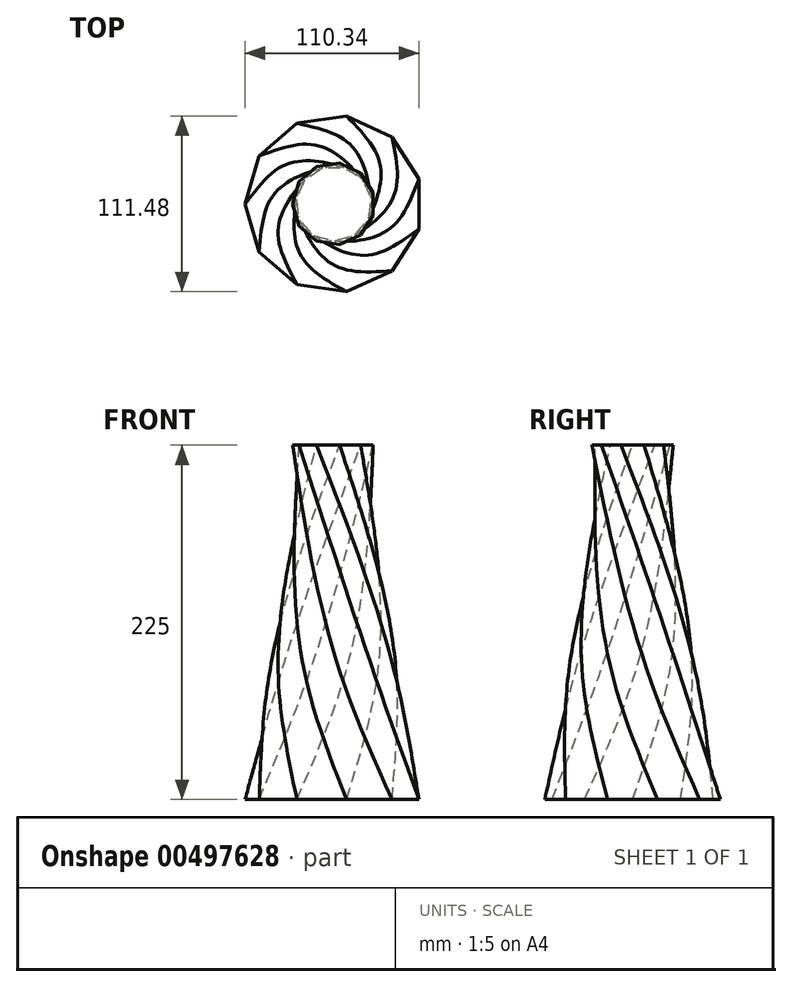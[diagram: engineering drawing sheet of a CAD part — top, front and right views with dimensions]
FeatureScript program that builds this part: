
annotation { "Feature Type Name" : "Feature", "Feature Type Description" : "" }
export const myFeature = defineFeature(function(context is Context, id is Id, definition is map)
    precondition{}
    {
        {
            var Q0;
            Q0=qCreatedBy(makeId("Top.planeOp"),FACE);
            var sketch = newSketch(context, id + "F0", { "sketchPlane" : qUnion([Q0])});
            skCircle(sketch, "E0.cCircle", {"center": v(0, 0) * mm, "radius": 40 * mm, "construction": true});
            skLineSegment(sketch, "E0.0", {"start": v(40, 11.75) * mm, "end": v(40, -11.75) * mm});
            skLineSegment(sketch, "E0.1", {"start": v(40, -11.75) * mm, "end": v(27.3, -31.5) * mm});
            skLineSegment(sketch, "E0.2", {"start": v(27.3, -31.5) * mm, "end": v(5.93, -41.26) * mm});
            skLineSegment(sketch, "E0.3", {"start": v(5.93, -41.26) * mm, "end": v(-17.32, -37.92) * mm});
            skLineSegment(sketch, "E0.4", {"start": v(-17.32, -37.92) * mm, "end": v(-35.07, -22.54) * mm});
            skLineSegment(sketch, "E0.5", {"start": v(-35.07, -22.54) * mm, "end": v(-41.69, 0) * mm});
            skLineSegment(sketch, "E0.6", {"start": v(-41.69, 0) * mm, "end": v(-35.07, 22.54) * mm});
            skLineSegment(sketch, "E0.7", {"start": v(-35.07, 22.54) * mm, "end": v(-17.32, 37.92) * mm});
            skLineSegment(sketch, "E0.8", {"start": v(-17.32, 37.92) * mm, "end": v(5.93, 41.26) * mm});
            skLineSegment(sketch, "E0.9", {"start": v(5.93, 41.26) * mm, "end": v(27.3, 31.5) * mm});
            skLineSegment(sketch, "E0.10", {"start": v(27.3, 31.5) * mm, "end": v(40, 11.75) * mm});
            skPoint(sketch, "E0.0.midPoint", {"position": v(40, 0) * mm});
            skSolve(sketch);
        }
        {
            var Q0;
            Q0=qCreatedBy(makeId("Top.planeOp"),FACE);
            cPlane(context, id + "F1", {"entities" : qUnion([Q0]), "cplaneType" : CPlaneType.OFFSET, "offset" : 150 * mm, "width" : 150 * mm, "height" : 150 * mm});
        }
        {
            var Q0;
            Q0=qCreatedBy(makeId("Top.planeOp"),FACE);
            cPlane(context, id + "F2", {"entities" : qUnion([Q0]), "cplaneType" : CPlaneType.OFFSET, "offset" : 75 * mm, "oppositeDirection" : true, "width" : 150 * mm, "height" : 150 * mm});
        }
        {
            var Q0;
            Q0=qCreatedBy(id+"F2.planeOp",FACE);
            var sketch = newSketch(context, id + "F3", { "sketchPlane" : qUnion([Q0])});
            skCircle(sketch, "E1.cCircle", {"center": v(0, 0) * mm, "radius": 54.03 * mm, "construction": true});
            skLineSegment(sketch, "E1.0", {"start": v(54.03, 15.86) * mm, "end": v(54.03, -15.86) * mm});
            skLineSegment(sketch, "E1.1", {"start": v(54.03, -15.86) * mm, "end": v(36.88, -42.56) * mm});
            skLineSegment(sketch, "E1.2", {"start": v(36.88, -42.56) * mm, "end": v(8.01, -55.74) * mm});
            skLineSegment(sketch, "E1.3", {"start": v(8.01, -55.74) * mm, "end": v(-23.4, -51.22) * mm});
            skLineSegment(sketch, "E1.4", {"start": v(-23.4, -51.22) * mm, "end": v(-47.37, -30.44) * mm});
            skLineSegment(sketch, "E1.5", {"start": v(-47.37, -30.44) * mm, "end": v(-56.31, 0) * mm});
            skLineSegment(sketch, "E1.6", {"start": v(-56.31, 0) * mm, "end": v(-47.37, 30.44) * mm});
            skLineSegment(sketch, "E1.7", {"start": v(-47.37, 30.44) * mm, "end": v(-23.4, 51.22) * mm});
            skLineSegment(sketch, "E1.8", {"start": v(-23.4, 51.22) * mm, "end": v(8.01, 55.74) * mm});
            skLineSegment(sketch, "E1.9", {"start": v(8.01, 55.74) * mm, "end": v(36.88, 42.56) * mm});
            skLineSegment(sketch, "E1.10", {"start": v(36.88, 42.56) * mm, "end": v(54.03, 15.86) * mm});
            skPoint(sketch, "E1.0.midPoint", {"position": v(54.03, 0) * mm});
            skSolve(sketch);
        }
        {
            var Q0;
            Q0=qCreatedBy(id+"F1.planeOp",FACE);
            var sketch = newSketch(context, id + "F4", { "sketchPlane" : qUnion([Q0])});
            skCircle(sketch, "E2.cCircle", {"center": v(0, 0) * mm, "radius": 25.02 * mm, "construction": true});
            skLineSegment(sketch, "E2.0", {"start": v(25.02, 7.35) * mm, "end": v(25.02, -7.35) * mm});
            skLineSegment(sketch, "E2.1", {"start": v(25.02, -7.35) * mm, "end": v(17.07, -19.7) * mm});
            skLineSegment(sketch, "E2.2", {"start": v(17.07, -19.7) * mm, "end": v(3.71, -25.8) * mm});
            skLineSegment(sketch, "E2.3", {"start": v(3.71, -25.8) * mm, "end": v(-10.83, -23.72) * mm});
            skLineSegment(sketch, "E2.4", {"start": v(-10.83, -23.72) * mm, "end": v(-21.93, -14.1) * mm});
            skLineSegment(sketch, "E2.5", {"start": v(-21.93, -14.1) * mm, "end": v(-26.07, 0) * mm});
            skLineSegment(sketch, "E2.6", {"start": v(-26.07, 0) * mm, "end": v(-21.93, 14.1) * mm});
            skLineSegment(sketch, "E2.7", {"start": v(-21.93, 14.1) * mm, "end": v(-10.83, 23.72) * mm});
            skLineSegment(sketch, "E2.8", {"start": v(-10.83, 23.72) * mm, "end": v(3.71, 25.8) * mm});
            skLineSegment(sketch, "E2.9", {"start": v(3.71, 25.8) * mm, "end": v(17.07, 19.7) * mm});
            skLineSegment(sketch, "E2.10", {"start": v(17.07, 19.7) * mm, "end": v(25.02, 7.35) * mm});
            skPoint(sketch, "E2.0.midPoint", {"position": v(25.02, 0) * mm});
            skSolve(sketch);
        }
        {
            var Q0;
            Q0=makeQuery(id+"F3.imprint","IMPRINT",FACE,{"disambiguationData":[TD([[makeQuery(id+"F3.imprint","IMPRINT",EDGE,{"derivedFrom":sQuery(id+"F3.wireOp",EDGE,"E1.0")}),-1.0]])]});
            var Q1;
            {var subQ3=sQuery(id+"F0.wireOp",EDGE,"E0.1");Q1=makeQuery(id+"F0.imprint","IMPRINT",FACE,{"disambiguationData":[TD([[makeQuery(id+"F0.imprint","IMPRINT",EDGE,{"derivedFrom":subQ3}),-1.0]])]});}
            var Q2;
            {var subQ3=sQuery(id+"F4.wireOp",EDGE,"E2.1");Q2=makeQuery(id+"F4.imprint","IMPRINT",FACE,{"disambiguationData":[TD([[makeQuery(id+"F4.imprint","IMPRINT",EDGE,{"derivedFrom":subQ3}),-1.0]])]});}
            var Q3;
            Q3=sQuery(id+"F3.wireOp",VERTEX,"E1.6.start");
            var Q4;
            Q4=sQuery(id+"F0.wireOp",VERTEX,"E0.7.start");
            var Q5;
            Q5=sQuery(id+"F4.wireOp",VERTEX,"E2.10.start");
            loft(context, id + "F5", {"sheetProfilesArray" : [{ "sheetProfileEntities" : qUnion([Q0]) }, { "sheetProfileEntities" : qUnion([Q1]) }, { "sheetProfileEntities" : qUnion([Q2]) }], "matchConnections" : true, "connections" : [{ "connectionEntities" : qUnion([Q3, Q4, Q5]), "connectionEdgeQueries" : qUnion([]), "connectionEdgeParameters" : [] }]});
        }
    });
